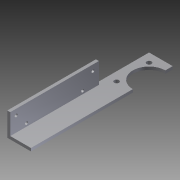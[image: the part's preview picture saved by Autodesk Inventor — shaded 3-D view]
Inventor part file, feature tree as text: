
AUTODESK INVENTOR PART (.ipt)
format: ipt  version: 2012 (Build 160160000, 160)  size: 124,416 bytes
history: native  units: in
note: dims shown in document units (in); Inventor stores cm internally (conversion verified against a paired STEP export)
features: extrude x4, sketch x4, other x3
ambient origin geometry x8: Origin, YZ Plane, XZ Plane, XY Plane, X Axis, Y Axis, Z Axis, Center Point
bodies: Solid1 (feature_tree)
feature tree (11):
  other  "8 ball corner L.ipt"
  extrude  "Extrusion1"  Depth=1.5in TaperAngle=0.0deg
  sketch  "Sketch3"  dims[d5=1.0in d6=0.125in]
  extrude  "Extrusion2"  Depth=0.375in
  extrude  "Extrusion3"  Depth=0.125in
  extrude  "Extrusion4"  Depth=0.375in
  other  "Solid1::8 ball corner L.ipt"
  sketch  "Sketch1"  dims[d0=0.3937in d1=1.5in d2=0.0in]
  sketch  "Sketch2"  dims[d3=0.25in d4=0.375in]
  other  "TaggingFeature1"
  sketch  "Sketch4"  dims[d7=0.375in d8=0.375in d9=0.125in d10=0.0in d11=0.125in d12=0.0in d13=0.125in d14=0.25in d15=0.25in d16=0.6875in d17=0.75in d18=0.125in d19=0.0in]
